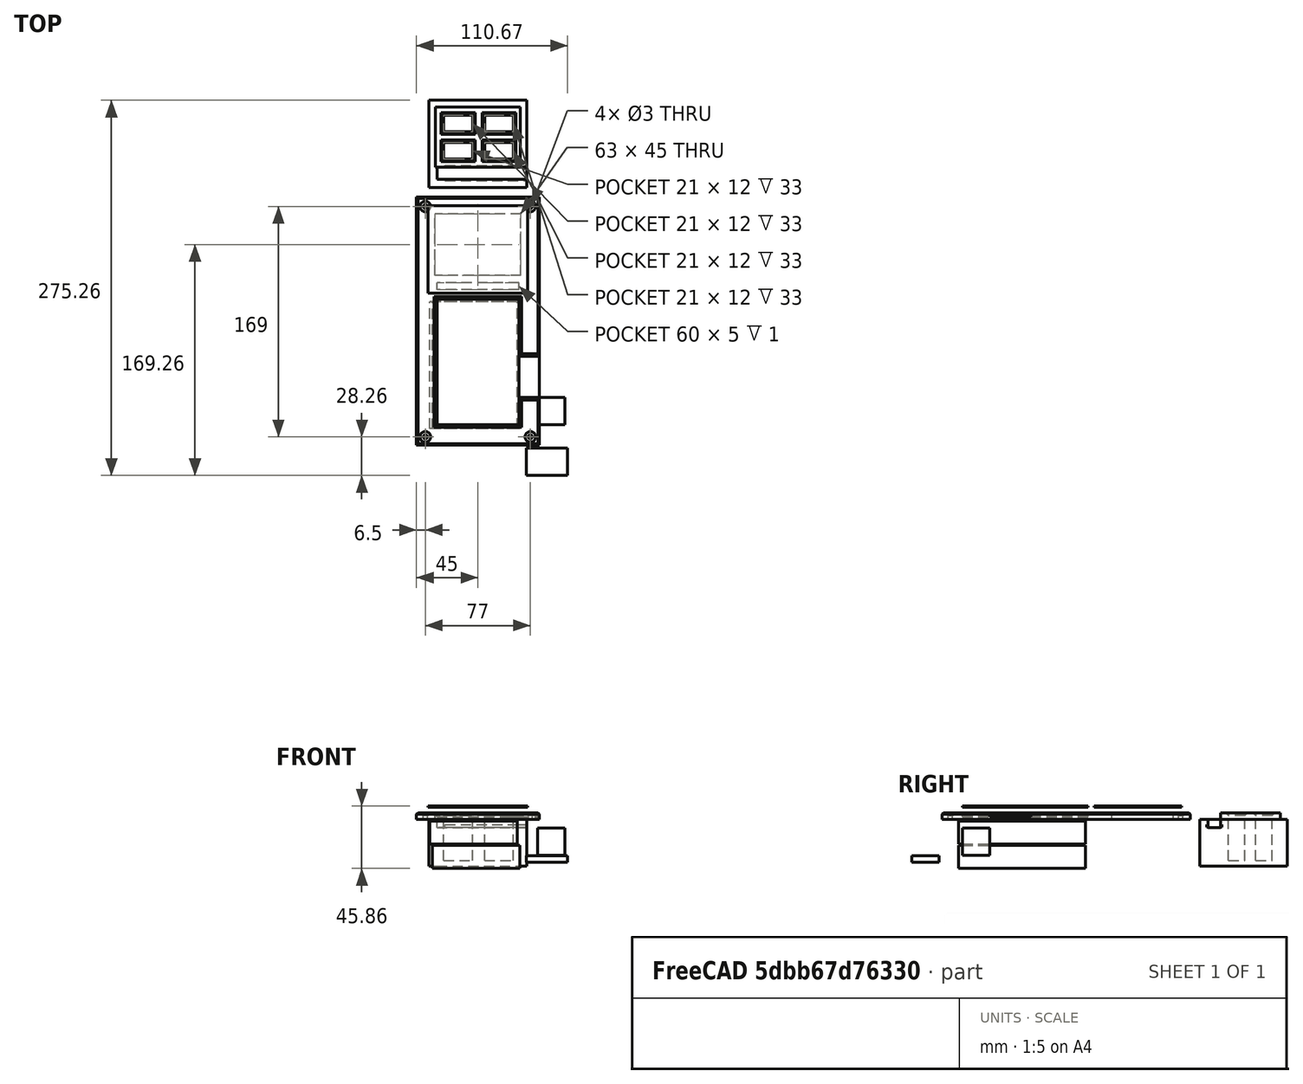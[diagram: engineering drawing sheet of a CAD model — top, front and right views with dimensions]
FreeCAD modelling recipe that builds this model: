
FCSTD DOCUMENT  (FreeCAD 0.15R4671 (Git))
Label: deckel_neu
License: All rights reserved
LicenseURL: http://en.wikipedia.org/wiki/All_rights_reserved
objects: Part::Box×20, Part::MultiFuse×6, Part::FeaturePython×6, Part::Cut×6, Part::Chamfer×2, Part::Cylinder×1, Part::Cone×1, App::MeasureDistance×1
note: 42 computed .brp shape members not serialized (recipe doc carries the construction recipe); baked Part::Feature solids carry a one-line shape summary decoded from their .brp

FEATURE [Part::Box] Box  label="Cube"
  Height = 4
  Length = 60
  Width = 92
FEATURE [Part::Box] Box001  label="Fingergriff"
  Height = 4
  Length = 30
  Placement = pos=(50,20,0) rot=(0,0,1;0rad)
  Width = 30
FEATURE [Part::MultiFuse] Fusion
  Shapes = -> [Box001,Box]
FEATURE [Part::Box] Box002  label="Cube001"
  Height = 35
  Length = 21
  Width = 12
FEATURE [Part::Box] Box003  label="Cube002"
  Height = 4
  Length = 25
  Placement = pos=(-2,-2,32) rot=(0,0,1;0rad)
  Width = 16
FEATURE [Part::Chamfer] Chamfer001
  Base = -> Box003
  Edges = 4 edges r=3: [Edge4,Edge8,Edge9,Edge11]
FEATURE [Part::MultiFuse] Fusion001  label="USBStickAussparung"
  Placement = pos=(30,175,0) rot=(0,0,1;0rad)
  Shapes = -> [Box002,Chamfer001]
FEATURE [Part::FeaturePython] Clone  label="Clone of USBStickAussparung"  # Draft clone (typed FeaturePython)
  Objects = -> [Fusion001]
  Placement = pos=(30,155,0) rot=(0,0,1;0rad)
  Scale = (1,1,1)
FEATURE [Part::FeaturePython] Clone001  label="Clone of USBStickAussparung001"  # Draft clone (typed FeaturePython)
  Objects = -> [Fusion001]
  Placement = pos=(0,175,0) rot=(0,0,1;0rad)
  Scale = (1,1,1)
FEATURE [Part::FeaturePython] Clone002  label="Clone of USBStickAussparung002"  # Draft clone (typed FeaturePython)
  Objects = -> [Fusion001]
  Placement = pos=(0,155,0) rot=(0,0,1;0rad)
  Scale = (1,1,1)
FEATURE [Part::Box] Box004  label="Cube003"
  Height = 39
  Length = 62
  Placement = pos=(-1,149,0) rot=(0,0,1;0rad)
  Width = 44
FEATURE [Part::MultiFuse] Fusion002  label="USBAussparungen"
  Placement = pos=(5,0,4) rot=(0,0,1;0rad)
  Shapes = -> [Clone002,Fusion001,Clone001,Clone]
FEATURE [Part::Cut] Cut  label="USBHalter"
  Base = -> Box004
  Placement = pos=(0,40,-36) rot=(0,0,1;0rad)
  Tool = -> Fusion002
FEATURE [Part::Box] Box005  label="Cube004"
  Height = 39
  Length = 63
  Placement = pos=(-1.5,109.5,-10) rot=(0,0,1;0rad)
  Width = 45
FEATURE [Part::Box] Box006  label="Cube005"
  Height = 5
  Length = 90
  Placement = pos=(-15,-15,-2) rot=(0,0,1;0rad)
  Width = 182
FEATURE [Part::Box] Box007  label="Cube006"
  Height = 34
  Length = 72
  Placement = pos=(-6,174,-36) rot=(0,0,1;0rad)
  Width = 6
FEATURE [Part::Box] Box008  label="Cube007"
  Height = 34
  Length = 6
  Placement = pos=(-6,174,-36) rot=(0,0,1;0rad)
  Width = 64
FEATURE [Part::Box] Box009  label="Cube008"
  Height = 34
  Length = 6
  Placement = pos=(60,189,-36) rot=(0,0,1;0rad)
  Width = 49
FEATURE [Part::Box] Box010  label="Cube009"
  Height = 34
  Length = 72
  Placement = pos=(-6,230,-36) rot=(0,0,1;0rad)
  Width = 8
FEATURE [Part::Box] Box011  label="Cube010"
  Height = 1.9
  Length = 60
  Placement = pos=(6,179,-7.5) rot=(0,0,1;0rad)
  Width = 11
FEATURE [Part::Box] Box012  label="Cube011"
  Height = 28
  Length = 72
  Placement = pos=(-6,174,-36) rot=(0,0,1;0rad)
  Width = 15
FEATURE [Part::MultiFuse] Fusion003
  Shapes = -> [Box012,Box010,Box009,Box008,Box007,Cut]
FEATURE [Part::Cut] Cut003  label="HalterBlock"
  Base = -> Fusion003
  Tool = -> Box011
FEATURE [Part::Cut] Cut004
  Base = -> Box006
  Tool = -> Box005
FEATURE [Part::Cut] Cut005
  Base = -> Cut004
  Tool = -> Fusion
FEATURE [Part::Box] Box013  label="LEDAnzeige"
  Height = 10
  Length = 60
  Placement = pos=(0,99,2) rot=(0,0,1;0rad)
  Width = 5
FEATURE [Part::Box] Box014  label="RaspberryPiA"
  Height = 17
  Length = 93
  Placement = pos=(60.6141,-2.96352,-37.8551) rot=(0,0,1;1.5708rad)
  Width = 64
FEATURE [Part::Box] Box016  label="Teensy"
  Height = 5
  Length = 30
  Placement = pos=(65.6717,-37.258,-33.4108) rot=(0,0,1;0rad)
  Width = 20
FEATURE [Part::Box] Box017  label="RFID CardReader"
  Height = 17
  Length = 93
  Placement = pos=(58.8508,-2.79585,-20) rot=(0,0,1;1.5708rad)
  Width = 64
FEATURE [Part::Box] Box018  label="Summer"
  Height = 20
  Length = 20
  Placement = pos=(73.759,-0.000131875,-28.247) rot=(0,0,1;0rad)
  Width = 20
FEATURE [Part::Cylinder] Cylinder
  Angle = 360
  Height = 10
  Placement = pos=(-8.5,-9,-5) rot=(0,0,1;0rad)
  Radius = 1.5
FEATURE [Part::Cone] Cone
  Angle = 360
  Height = 2
  Placement = pos=(-8.5,-9,1.1) rot=(0,0,1;0rad)
  Radius1 = 1.5
  Radius2 = 4
FEATURE [Part::MultiFuse] Fusion004
  Shapes = -> [Cylinder,Cone]
FEATURE [Part::FeaturePython] Clone006  label="Clone of Fusion004"  # Draft clone (typed FeaturePython)
  Objects = -> [Fusion004]
  Placement = pos=(77,0,0) rot=(0,0,1;0rad)
  Scale = (1,1,1)
FEATURE [Part::FeaturePython] Clone007  label="Clone of Fusion005"  # Draft clone (typed FeaturePython)
  Objects = -> [Fusion004]
  Placement = pos=(77,169,0) rot=(0,0,1;0rad)
  Scale = (1,1,1)
FEATURE [Part::FeaturePython] Clone008  label="Clone of Fusion006"  # Draft clone (typed FeaturePython)
  Objects = -> [Fusion004]
  Placement = pos=(0,169,0) rot=(0,0,1;0rad)
  Scale = (1,1,1)
FEATURE [Part::MultiFuse] Fusion005  label="Schraubloecher"
  Shapes = -> [Clone008,Clone007,Clone006,Fusion004]
FEATURE [Part::Cut] Cut006
  Base = -> Cut005
  Tool = -> Box013
FEATURE [Part::Cut] Cut007
  Base = -> Cut006
  Tool = -> Fusion005
FEATURE [Part::Chamfer] Chamfer  label="Kartenablage"
  Base = -> Cut007
  Edges = 12 edges: [Edge2 r=1,Edge7 r=1,Edge8 r=1,Edge9 r=1,Edge10 r=2,Edge11 r=2,Edge12 r=1,Edge13 r=2,Edge14 r=2,Edge15 r=2,Edge16 r=2,Edge17 r=2]
FEATURE [Part::Box] Box019  label="AussparungLasercutBox"
  Height = 1
  Length = 73
  Placement = pos=(-6.5,96.5,7) rot=(0,0,1;0rad)
  Width = 64
FEATURE [Part::Box] Box020  label="AussparungLasercutBox001"
  Height = 1
  Length = 60
  Placement = pos=(0,0,7) rot=(0,0,1;0rad)
  Width = 92
FEATURE [App::MeasureDistance] Distance  label="Distance: 5.000"
  Distance = 5.00028
  P1 = (1.30941,233,-1.98352)
  P2 = (1.25936,238,-2)
